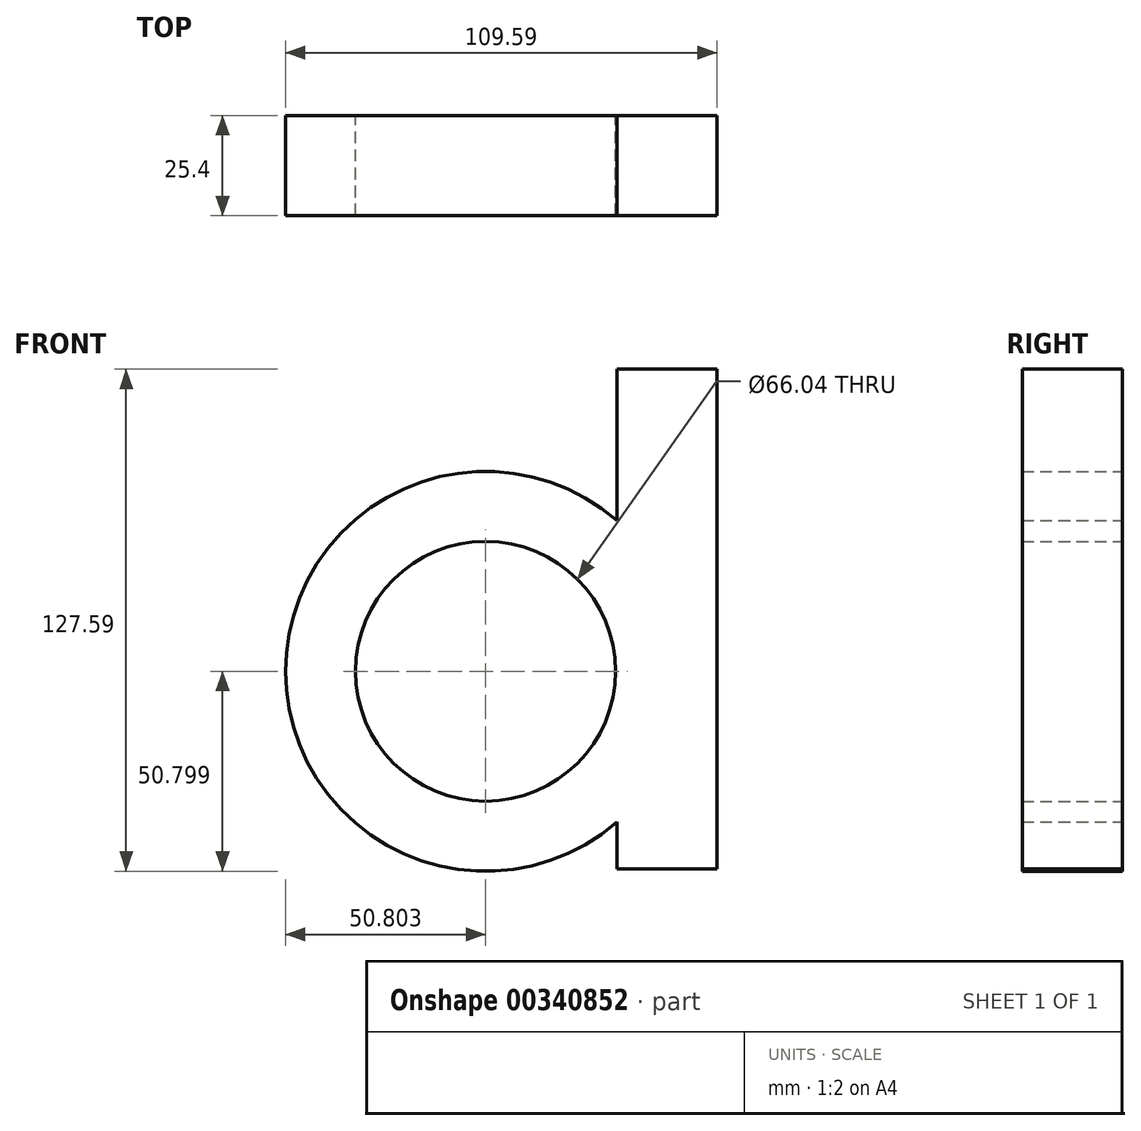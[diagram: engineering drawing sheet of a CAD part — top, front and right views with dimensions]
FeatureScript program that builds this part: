
annotation { "Feature Type Name" : "Feature", "Feature Type Description" : "" }
export const myFeature = defineFeature(function(context is Context, id is Id, definition is map)
    precondition{}
    {
        {
            var Q0;
            Q0=qCreatedBy(makeId("Front.planeOp"),FACE);
            var sketch = newSketch(context, id + "F0", { "sketchPlane" : qUnion([Q0])});
            skLineSegment(sketch, "E0.bottom", {"start": v(63.18, 62.21) * mm, "end": v(37.78, 62.21) * mm});
            skLineSegment(sketch, "E0.top", {"start": v(63.18, -64.79) * mm, "end": v(37.78, -64.79) * mm});
            skLineSegment(sketch, "E0.left", {"start": v(63.18, 62.21) * mm, "end": v(63.18, -64.79) * mm});
            skLineSegment(sketch, "E0.right", {"start": v(37.78, 62.21) * mm, "end": v(37.78, -64.79) * mm});
            skArc(sketch, "E1", {"start": v(51.17, 5.23) * mm, "mid": v(-46.13, -9.24) * mm, "end": v(46, -43.73) * mm});
            skArc(sketch, "E2", {"start": v(35.96, -4.9) * mm, "mid": v(-28.63, -14.7) * mm, "end": v(36.02, -24.06) * mm});
            skSolve(sketch);
        }
        {
            var Q0;
            {var subQ1=sQuery(id+"F0.wireOp",EDGE,"E0.bottom");Q0=makeQuery(id+"F0.imprint","IMPRINT",FACE,{"disambiguationData":[TD([[makeQuery(id+"F0.imprint","IMPRINT",EDGE,{"derivedFrom":subQ1}),1.0]])]});}
            var Q1;
            {var subQ0=sQuery(id+"F0.wireOp",EDGE,"E1");var subQ1=sQuery(id+"F0.wireOp",EDGE,"E0.right");var subQ2=makeQuery(id+"F0.imprint","INTERSECT",VERTEX,{"disambiguationData":[OD(0.0)],"derivedFrom":[subQ1,subQ0]});Q1=makeQuery(id+"F0.imprint","IMPRINT",FACE,{"disambiguationData":[TD([[makeQuery(id+"F0.imprint","IMPRINT",EDGE,{"disambiguationData":[TD([[subQ2,-1.0]])],"derivedFrom":subQ1}),-1.0]])]});}
            extrude(context, id + "F1", {"entities" : qUnion([Q0, Q1]), "depth" : 25.4 * mm});
        }
        {
            var Q0;
            Q0=sQuery(id+"F0.wireOp",VERTEX,"E1.center");
            var Q1;
            Q1=makeQuery(id+"F1.opExtrude","SWEPT_BODY",BODY,{"disambiguationData":[OSD([sQuery(id+"F0.wireOp",EDGE,"E0.bottom"),sQuery(id+"F0.wireOp",EDGE,"E0.top"),sQuery(id+"F0.wireOp",EDGE,"E0.left"),sQuery(id+"F0.wireOp",EDGE,"E0.right"),sQuery(id+"F0.wireOp",EDGE,"E1")])]});
            hole(context, id + "F2", {"style" : HoleStyle.SIMPLE, "endStyle" : HoleEndStyle.THROUGH, "oppositeDirection" : true, "holeDiameter" : 66.04 * mm, "tappedDepth" : 12.7 * mm, "tapClearance" : 3, "locations" : qUnion([Q0]), "scope" : qUnion([Q1])});
        }
    });
